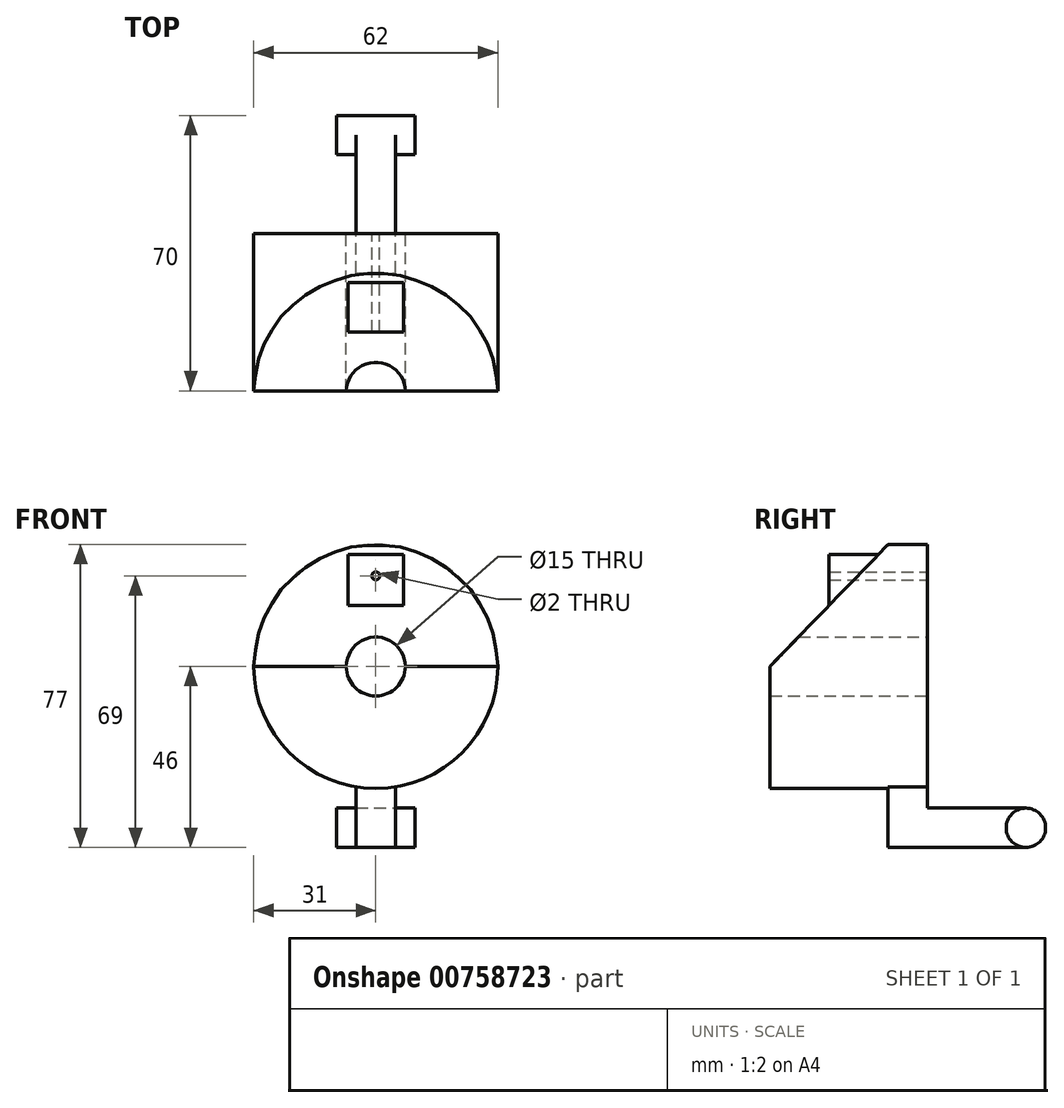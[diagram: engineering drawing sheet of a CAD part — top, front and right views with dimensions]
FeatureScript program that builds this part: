
annotation { "Feature Type Name" : "Feature", "Feature Type Description" : "" }
export const myFeature = defineFeature(function(context is Context, id is Id, definition is map)
    precondition{}
    {
        {
            var Q0;
            Q0=qCreatedBy(makeId("Front.planeOp"),FACE);
            var sketch = newSketch(context, id + "F0", { "sketchPlane" : qUnion([Q0])});
            skCircle(sketch, "E0", {"center": v(0, 0) * mm, "radius": 31 * mm});
            skCircle(sketch, "E1", {"center": v(0, 0) * mm, "radius": 7.5 * mm});
            skLineSegment(sketch, "E2", {"start": v(0, 0) * mm, "end": v(-7.5, 0) * mm});
            skLineSegment(sketch, "E3", {"start": v(-7.5, 0) * mm, "end": v(-7.5, 30.08) * mm});
            skLineSegment(sketch, "E4", {"start": v(0, 0) * mm, "end": v(7.5, 0) * mm});
            skLineSegment(sketch, "E5", {"start": v(7.5, 0) * mm, "end": v(7.5, 30.08) * mm});
            skSolve(sketch);
        }
        {
            var Q0;
            {var subQ0=sQuery(id+"F0.wireOp",EDGE,"E3");Q0=makeQuery(id+"F0.imprint","IMPRINT",FACE,{"disambiguationData":[TD([[makeQuery(id+"F0.imprint","IMPRINT",EDGE,{"derivedFrom":subQ0}),1.0]])]});}
            var Q1;
            {var subQ0=sQuery(id+"F0.wireOp",EDGE,"E3");Q1=makeQuery(id+"F0.imprint","IMPRINT",FACE,{"disambiguationData":[TD([[makeQuery(id+"F0.imprint","IMPRINT",EDGE,{"derivedFrom":subQ0}),-1.0]])]});}
            extrude(context, id + "F1", {"entities" : qUnion([Q0, Q1]), "depth" : 40 * mm, "offsetDistance" : 25 * mm});
        }
        {
            var Q0;
            Q0=qCreatedBy(makeId("Right.planeOp"),FACE);
            var sketch = newSketch(context, id + "F2", { "sketchPlane" : qUnion([Q0])});
            skLineSegment(sketch, "E6", {"start": v(0, 0) * mm, "end": v(0, 31) * mm});
            skLineSegment(sketch, "E7", {"start": v(0, 31) * mm, "end": v(-10, 31) * mm});
            skLineSegment(sketch, "E8", {"start": v(-10, 31) * mm, "end": v(-40, 0) * mm});
            skLineSegment(sketch, "E9", {"start": v(-10, 31) * mm, "end": v(-40, 31) * mm});
            skLineSegment(sketch, "E10", {"start": v(-40, 31) * mm, "end": v(-40, 0) * mm});
            skSolve(sketch);
        }
        {
            var Q0;
            Q0=makeQuery(id+"F2.imprint","IMPRINT",FACE,{"disambiguationData":[TD([[makeQuery(id+"F2.imprint","IMPRINT",EDGE,{"derivedFrom":sQuery(id+"F2.wireOp",EDGE,"E8")}),-1.0]])]});
            extrude(context, id + "F3", {"entities" : qUnion([Q0]), "operationType" : NewBodyOperationType.REMOVE, "depth" : 44.8 * mm, "offsetDistance" : 25 * mm, "hasSecondDirection" : true, "secondDirectionOppositeDirection" : true, "secondDirectionDepth" : 52.7 * mm});
        }
        {
            var Q0;
            Q0=qCreatedBy(makeId("Front.planeOp"),FACE);
            var sketch = newSketch(context, id + "F4", { "sketchPlane" : qUnion([Q0])});
            skLineSegment(sketch, "E11", {"start": v(0, 0) * mm, "end": v(0, 23) * mm});
            skCircle(sketch, "E12", {"center": v(0, 23) * mm, "radius": 1 * mm});
            skLineSegment(sketch, "E13", {"start": v(0, 11.5) * mm, "end": v(7, 11.5) * mm});
            skLineSegment(sketch, "E14", {"start": v(0, 11.5) * mm, "end": v(-7, 11.5) * mm});
            skLineSegment(sketch, "E15", {"start": v(7, 11.5) * mm, "end": v(7, 28.5) * mm});
            skLineSegment(sketch, "E16", {"start": v(7, 28.5) * mm, "end": v(-7, 28.5) * mm});
            skLineSegment(sketch, "E17", {"start": v(-7, 28.5) * mm, "end": v(-7, 11.5) * mm});
            skCircle(sketch, "E18.0", {"center": v(0, 0) * mm, "radius": 7.5 * mm});
            skLineSegment(sketch, "E19", {"start": v(-7, 11.5) * mm, "end": v(-7, 2.7) * mm});
            skLineSegment(sketch, "E20", {"start": v(7, 11.5) * mm, "end": v(7, 2.7) * mm});
            skSolve(sketch);
        }
        {
            var Q0;
            Q0=makeQuery(id+"F4.imprint","IMPRINT",FACE,{"disambiguationData":[TD([[makeQuery(id+"F4.imprint","IMPRINT",EDGE,{"derivedFrom":sQuery(id+"F4.wireOp",EDGE,"E12")}),1.0]])]});
            extrude(context, id + "F5", {"entities" : qUnion([Q0]), "operationType" : NewBodyOperationType.REMOVE, "depth" : 25 * mm, "offsetDistance" : 25 * mm});
        }
        {
            var Q0;
            Q0 = qSketchRegion(id + "F4", true);
            extrude(context, id + "F6", {"entities" : qUnion([Q0]), "operationType" : NewBodyOperationType.ADD, "depth" : 25 * mm, "offsetDistance" : 25 * mm});
        }
        {
            var Q0;
            Q0=makeQuery(id+"F6.boolean.opBoolean","SPLIT",FACE,{"disambiguationData":[TD([makeQuery(id+"F1.opExtrude","SWEPT_FACE",FACE,{"disambiguationData":[OSD([sQuery(id+"F0.wireOp",EDGE,"E1")])]})])],"derivedFrom":makeQuery(id+"F6.opExtrude","CAP_FACE",FACE,{"disambiguationData":[OSD([sQuery(id+"F4.wireOp",EDGE,"E12"),sQuery(id+"F4.wireOp",EDGE,"E15"),sQuery(id+"F4.wireOp",EDGE,"E16"),sQuery(id+"F4.wireOp",EDGE,"E17"),sQuery(id+"F4.wireOp",EDGE,"E18.0"),sQuery(id+"F4.wireOp",EDGE,"E19"),sQuery(id+"F4.wireOp",EDGE,"E20")])],"isStart":false})});
            extrude(context, id + "F7", {"entities" : qUnion([Q0]), "operationType" : NewBodyOperationType.REMOVE, "oppositeDirection" : true, "depth" : 41 * mm, "offsetDistance" : 25 * mm});
        }
        {
            var Q0;
            Q0=qCreatedBy(makeId("Front.planeOp"),FACE);
            var sketch = newSketch(context, id + "F8", { "sketchPlane" : qUnion([Q0])});
            skLineSegment(sketch, "E21", {"start": v(0, 0) * mm, "end": v(5, 0) * mm});
            skLineSegment(sketch, "E22", {"start": v(5, 0) * mm, "end": v(5, -46) * mm});
            skLineSegment(sketch, "E23", {"start": v(0, 0) * mm, "end": v(-5, 0) * mm});
            skLineSegment(sketch, "E24", {"start": v(-5, 0) * mm, "end": v(-5, -46) * mm});
            skLineSegment(sketch, "E25", {"start": v(-5, -46) * mm, "end": v(5, -46) * mm});
            skLineSegment(sketch, "E26", {"start": v(0, -46) * mm, "end": v(0, -36) * mm});
            skLineSegment(sketch, "E27", {"start": v(0, -36) * mm, "end": v(-5, -36) * mm});
            skLineSegment(sketch, "E28", {"start": v(0, -36) * mm, "end": v(5, -36) * mm});
            skCircle(sketch, "E29.0", {"center": v(0, 0) * mm, "radius": 7.5 * mm});
            skCircle(sketch, "E30", {"center": v(0, 0) * mm, "radius": 11.5 * mm});
            skLineSegment(sketch, "E31", {"start": v(0, -36) * mm, "end": v(0, -31) * mm});
            skSolve(sketch);
        }
        {
            var Q0;
            {var subQ0=sQuery(id+"F8.wireOp",EDGE,"E27");Q0=makeQuery(id+"F8.imprint","IMPRINT",FACE,{"disambiguationData":[TD([[makeQuery(id+"F8.imprint","IMPRINT",EDGE,{"derivedFrom":subQ0}),-1.0]])]});}
            var Q1;
            {var subQ4=sQuery(id+"F8.wireOp",EDGE,"E26");Q1=makeQuery(id+"F8.imprint","IMPRINT",FACE,{"disambiguationData":[TD([[makeQuery(id+"F8.imprint","IMPRINT",EDGE,{"derivedFrom":subQ4}),-1.0]])]});}
            var Q2;
            {var subQ4=sQuery(id+"F8.wireOp",EDGE,"E26");Q2=makeQuery(id+"F8.imprint","IMPRINT",FACE,{"disambiguationData":[TD([[makeQuery(id+"F8.imprint","IMPRINT",EDGE,{"derivedFrom":subQ4}),1.0]])]});}
            extrude(context, id + "F9", {"entities" : qUnion([Q0, Q1, Q2]), "operationType" : NewBodyOperationType.ADD, "depth" : 10 * mm, "offsetDistance" : 25 * mm});
        }
        {
            var Q0;
            {var subQ4=sQuery(id+"F8.wireOp",EDGE,"E26");Q0=makeQuery(id+"F8.imprint","IMPRINT",FACE,{"disambiguationData":[TD([[makeQuery(id+"F8.imprint","IMPRINT",EDGE,{"derivedFrom":subQ4}),-1.0]])]});}
            var Q1;
            {var subQ4=sQuery(id+"F8.wireOp",EDGE,"E26");Q1=makeQuery(id+"F8.imprint","IMPRINT",FACE,{"disambiguationData":[TD([[makeQuery(id+"F8.imprint","IMPRINT",EDGE,{"derivedFrom":subQ4}),1.0]])]});}
            extrude(context, id + "F10", {"entities" : qUnion([Q0, Q1]), "operationType" : NewBodyOperationType.ADD, "oppositeDirection" : true, "depth" : 30 * mm, "offsetDistance" : 25 * mm});
        }
        {
            var Q0;
            {var subQ0=sQuery(id+"F8.wireOp",EDGE,"E22");Q0=makeQuery(id+"F10.boolean.opBoolean","MERGE",FACE,{"derivedFrom":[makeQuery(id+"F9.opExtrude","SWEPT_FACE",FACE,{"disambiguationData":[OSD([subQ0])]}),makeQuery(id+"F10.opExtrude","SWEPT_FACE",FACE,{"disambiguationData":[OSD([subQ0])]})]});}
            var sketch = newSketch(context, id + "F11", { "sketchPlane" : qUnion([Q0])});
            skLineSegment(sketch, "E32", {"start": v(0, 0) * mm, "end": v(0, -41) * mm});
            skLineSegment(sketch, "E33", {"start": v(0, -41) * mm, "end": v(30, -41) * mm});
            skCircle(sketch, "E34", {"center": v(25, -41) * mm, "radius": 5 * mm});
            skLineSegment(sketch, "E35", {"start": v(0, 0) * mm, "end": v(0, -23) * mm});
            skLineSegment(sketch, "E36", {"start": v(0, -23) * mm, "end": v(0, -41) * mm});
            skSolve(sketch);
        }
        {
            var Q0;
            {var subQ0=sQuery(id+"F11.wireOp",EDGE,"E34");var subQ1=sQuery(id+"F8.wireOp",EDGE,"E22");var subQ2=makeQuery(id+"F10.opExtrude","CAP_EDGE",EDGE,{"disambiguationData":[OSD([subQ1])],"isStart":false});var subQ3=makeQuery(id+"F11.imprint","INTERSECT",VERTEX,{"derivedFrom":[subQ2,sQuery(id+"F11.wireOp",EDGE,"E33"),subQ0]});Q0=makeQuery(id+"F11.imprint","IMPRINT",FACE,{"disambiguationData":[TD([[makeQuery(id+"F11.imprint","IMPRINT",EDGE,{"disambiguationData":[TD([[subQ3,-1.0]])],"derivedFrom":subQ0}),-1.0]])]});}
            var Q1;
            {var subQ0=sQuery(id+"F11.wireOp",EDGE,"E34");var subQ1=sQuery(id+"F8.wireOp",EDGE,"E22");var subQ2=makeQuery(id+"F10.opExtrude","CAP_EDGE",EDGE,{"disambiguationData":[OSD([subQ1])],"isStart":false});var subQ3=makeQuery(id+"F11.imprint","INTERSECT",VERTEX,{"derivedFrom":[subQ2,sQuery(id+"F11.wireOp",EDGE,"E33"),subQ0]});Q1=makeQuery(id+"F11.imprint","IMPRINT",FACE,{"disambiguationData":[TD([[makeQuery(id+"F11.imprint","IMPRINT",EDGE,{"disambiguationData":[TD([[subQ3,1.0]])],"derivedFrom":subQ0}),-1.0]])]});}
            extrude(context, id + "F12", {"entities" : qUnion([Q0, Q1]), "operationType" : NewBodyOperationType.REMOVE, "oppositeDirection" : true, "depth" : 25 * mm, "offsetDistance" : 25 * mm});
        }
        {
            var Q0;
            {var subQ0=sQuery(id+"F11.wireOp",EDGE,"E34");var subQ1=sQuery(id+"F11.wireOp",EDGE,"E33");var subQ4=makeQuery(id+"F11.imprint","INTERSECT",VERTEX,{"derivedFrom":[subQ1,subQ0]});Q0=makeQuery(id+"F11.imprint","IMPRINT",FACE,{"disambiguationData":[TD([[makeQuery(id+"F11.imprint","IMPRINT",EDGE,{"disambiguationData":[TD([[subQ4,-1.0]])],"derivedFrom":subQ1}),-1.0]])]});}
            var Q1;
            {var subQ0=sQuery(id+"F11.wireOp",EDGE,"E34");var subQ1=sQuery(id+"F11.wireOp",EDGE,"E33");var subQ4=makeQuery(id+"F11.imprint","INTERSECT",VERTEX,{"derivedFrom":[subQ1,subQ0]});Q1=makeQuery(id+"F11.imprint","IMPRINT",FACE,{"disambiguationData":[TD([[makeQuery(id+"F11.imprint","IMPRINT",EDGE,{"disambiguationData":[TD([[subQ4,-1.0]])],"derivedFrom":subQ1}),1.0]])]});}
            extrude(context, id + "F13", {"entities" : qUnion([Q0, Q1]), "operationType" : NewBodyOperationType.ADD, "depth" : 5 * mm, "offsetDistance" : 25 * mm, "hasSecondDirection" : true, "secondDirectionOppositeDirection" : true, "secondDirectionDepth" : 15 * mm});
        }
    });
